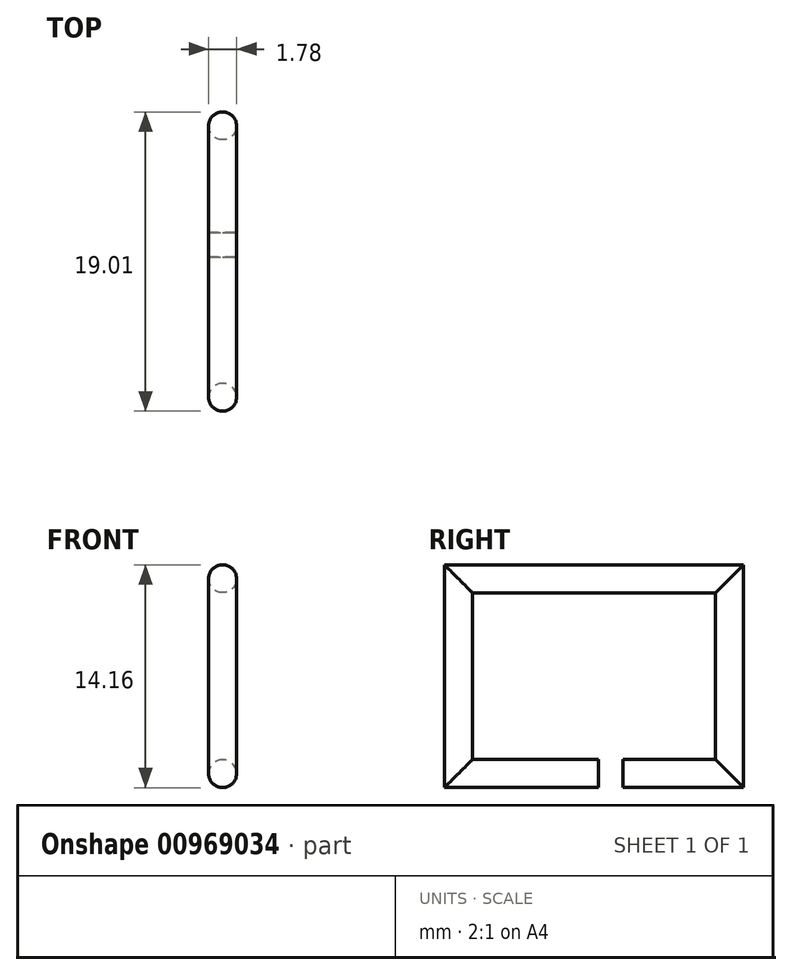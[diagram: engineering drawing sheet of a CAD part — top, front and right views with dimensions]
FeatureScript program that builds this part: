
annotation { "Feature Type Name" : "Feature", "Feature Type Description" : "" }
export const myFeature = defineFeature(function(context is Context, id is Id, definition is map)
    precondition{}
    {
        {
            var Q0;
            Q0=qCreatedBy(makeId("Front.planeOp"),FACE);
            var sketch = newSketch(context, id + "F0", { "sketchPlane" : qUnion([Q0])});
            skCircle(sketch, "E0", {"center": v(0, 0) * mm, "radius": 0.89 * mm});
            skSolve(sketch);
        }
        {
            var Q0;
            Q0=qCreatedBy(makeId("Right.planeOp"),FACE);
            var sketch = newSketch(context, id + "F1", { "sketchPlane" : qUnion([Q0])});
            skLineSegment(sketch, "E1", {"start": v(0, 0) * mm, "end": v(-8.89, 0) * mm});
            skLineSegment(sketch, "E2", {"start": v(-8.89, 12.38) * mm, "end": v(8.34, 12.38) * mm});
            skLineSegment(sketch, "E3", {"start": v(8.34, 12.38) * mm, "end": v(8.34, 0) * mm});
            skLineSegment(sketch, "E4", {"start": v(-8.9, 12.38) * mm, "end": v(-8.9, 0) * mm});
            skLineSegment(sketch, "E5", {"start": v(8.34, 0) * mm, "end": v(1.58, 0) * mm});
            skSolve(sketch);
        }
        {
            var Q0;
            Q0=makeQuery(id+"F0.imprint","IMPRINT",FACE,{"disambiguationData":[TD([[makeQuery(id+"F0.imprint","IMPRINT",EDGE,{"derivedFrom":sQuery(id+"F0.wireOp",EDGE,"E0")}),1.0]])]});
            var Q1;
            Q1=sQuery(id+"F1.wireOp",EDGE,"E1");
            var Q2;
            Q2=sQuery(id+"F1.wireOp",EDGE,"E4");
            var Q3;
            Q3=sQuery(id+"F1.wireOp",EDGE,"E2");
            var Q4;
            Q4=sQuery(id+"F1.wireOp",EDGE,"E3");
            var Q5;
            Q5=sQuery(id+"F1.wireOp",EDGE,"E5");
            sweep(context, id + "F2", {"profiles" : qUnion([Q0]), "path" : qUnion([Q1, Q2, Q3, Q4, Q5])});
        }
    });
